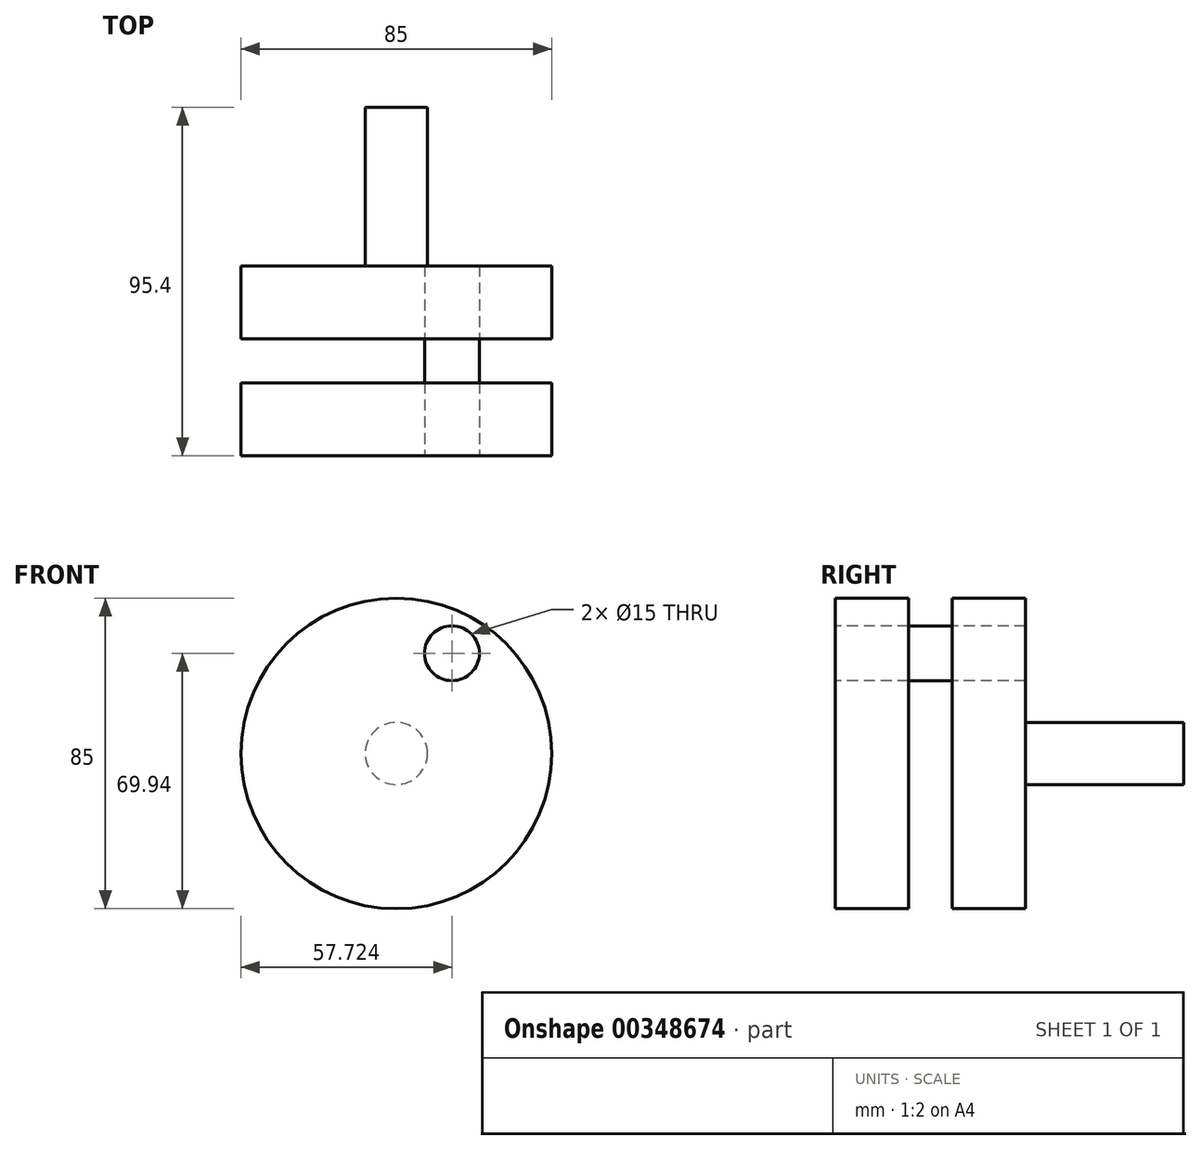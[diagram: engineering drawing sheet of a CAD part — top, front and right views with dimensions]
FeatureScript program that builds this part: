
annotation { "Feature Type Name" : "Feature", "Feature Type Description" : "" }
export const myFeature = defineFeature(function(context is Context, id is Id, definition is map)
    precondition{}
    {
        {
            var Q0;
            Q0=qCreatedBy(makeId("Front.planeOp"),FACE);
            var sketch = newSketch(context, id + "F0", { "sketchPlane" : qUnion([Q0])});
            skCircle(sketch, "E0", {"center": v(0, 0) * mm, "radius": 42.5 * mm});
            skSolve(sketch);
        }
        {
            var Q0;
            Q0=makeQuery(id+"F0.imprint","IMPRINT",FACE,{"disambiguationData":[TD([[makeQuery(id+"F0.imprint","IMPRINT",EDGE,{"derivedFrom":sQuery(id+"F0.wireOp",EDGE,"E0")}),1.0]])]});
            extrude(context, id + "F1", {"entities" : qUnion([Q0]), "depth" : 20 * mm});
        }
        {
            var Q0;
            Q0=makeQuery(id+"F1.opExtrude","CAP_FACE",FACE,{"disambiguationData":[OSD([sQuery(id+"F0.wireOp",EDGE,"E0")])],"isStart":false});
            cPlane(context, id + "F2", {"entities" : qUnion([Q0]), "cplaneType" : CPlaneType.OFFSET, "offset" : 12 * mm, "width" : 150 * mm, "height" : 150 * mm});
        }
        {
            var Q0;
            Q0=qCreatedBy(id+"F2.planeOp",FACE);
            var sketch = newSketch(context, id + "F3", { "sketchPlane" : qUnion([Q0])});
            skCircle(sketch, "E1", {"center": v(0, 0) * mm, "radius": 42.5 * mm});
            skSolve(sketch);
        }
        {
            var Q0;
            Q0=makeQuery(id+"F3.imprint","IMPRINT",FACE,{"disambiguationData":[TD([[makeQuery(id+"F3.imprint","IMPRINT",EDGE,{"derivedFrom":sQuery(id+"F3.wireOp",EDGE,"E1")}),1.0]])]});
            extrude(context, id + "F4", {"entities" : qUnion([Q0]), "depth" : 20 * mm});
        }
        {
            var Q0;
            Q0=makeQuery(id+"F1.opExtrude","CAP_FACE",FACE,{"disambiguationData":[OSD([sQuery(id+"F0.wireOp",EDGE,"E0")])],"isStart":true});
            var sketch = newSketch(context, id + "F5", { "sketchPlane" : qUnion([Q0])});
            skCircle(sketch, "E2", {"center": v(0, 0) * mm, "radius": 8.5 * mm});
            skSolve(sketch);
        }
        {
            var Q0;
            Q0=makeQuery(id+"F5.imprint","IMPRINT",FACE,{"disambiguationData":[TD([[makeQuery(id+"F5.imprint","IMPRINT",EDGE,{"derivedFrom":sQuery(id+"F5.wireOp",EDGE,"E2")}),1.0]])]});
            extrude(context, id + "F6", {"entities" : qUnion([Q0]), "operationType" : NewBodyOperationType.ADD, "depth" : 43.4 * mm});
        }
        {
            var Q0;
            Q0=makeQuery(id+"F4.opExtrude","CAP_FACE",FACE,{"disambiguationData":[OSD([sQuery(id+"F3.wireOp",EDGE,"E1")])],"isStart":false});
            var sketch = newSketch(context, id + "F7", { "sketchPlane" : qUnion([Q0])});
            skCircle(sketch, "E3", {"center": v(15.22, 27.44) * mm, "radius": 7.5 * mm});
            skSolve(sketch);
        }
        {
            var Q0;
            Q0=sQuery(id+"F7.wireOp",VERTEX,"E3.center");
            var Q1;
            Q1=makeQuery(id+"F1.opExtrude","SWEPT_BODY",BODY,{"disambiguationData":[OSD([sQuery(id+"F0.wireOp",EDGE,"E0")])]});
            var Q2;
            Q2=makeQuery(id+"F4.opExtrude","SWEPT_BODY",BODY,{"disambiguationData":[OSD([sQuery(id+"F3.wireOp",EDGE,"E1")])]});
            hole(context, id + "F8", {"style" : HoleStyle.SIMPLE, "endStyle" : HoleEndStyle.BLIND, "holeDiameter" : 15 * mm, "holeDepth" : 80 * mm, "isTappedThrough" : true, "tappedDepth" : 12 * mm, "tapClearance" : 3, "startFromSketch" : true, "locations" : qUnion([Q0]), "scope" : qUnion([Q1, Q2])});
        }
        {
            var Q0;
            Q0=makeQuery(id+"F4.opExtrude","CAP_FACE",FACE,{"disambiguationData":[OSD([sQuery(id+"F3.wireOp",EDGE,"E1")])],"isStart":false});
            var sketch = newSketch(context, id + "F9", { "sketchPlane" : qUnion([Q0])});
            skCircle(sketch, "E4", {"center": v(15.22, 27.44) * mm, "radius": 7.5 * mm});
            skSolve(sketch);
        }
        {
            var Q0;
            Q0=makeQuery(id+"F9.imprint","IMPRINT",FACE,{"disambiguationData":[TD([[makeQuery(id+"F9.imprint","IMPRINT",EDGE,{"derivedFrom":sQuery(id+"F9.wireOp",EDGE,"E4")}),1.0]])]});
            extrude(context, id + "F10", {"entities" : qUnion([Q0]), "oppositeDirection" : true, "depth" : 52 * mm});
        }
    });
